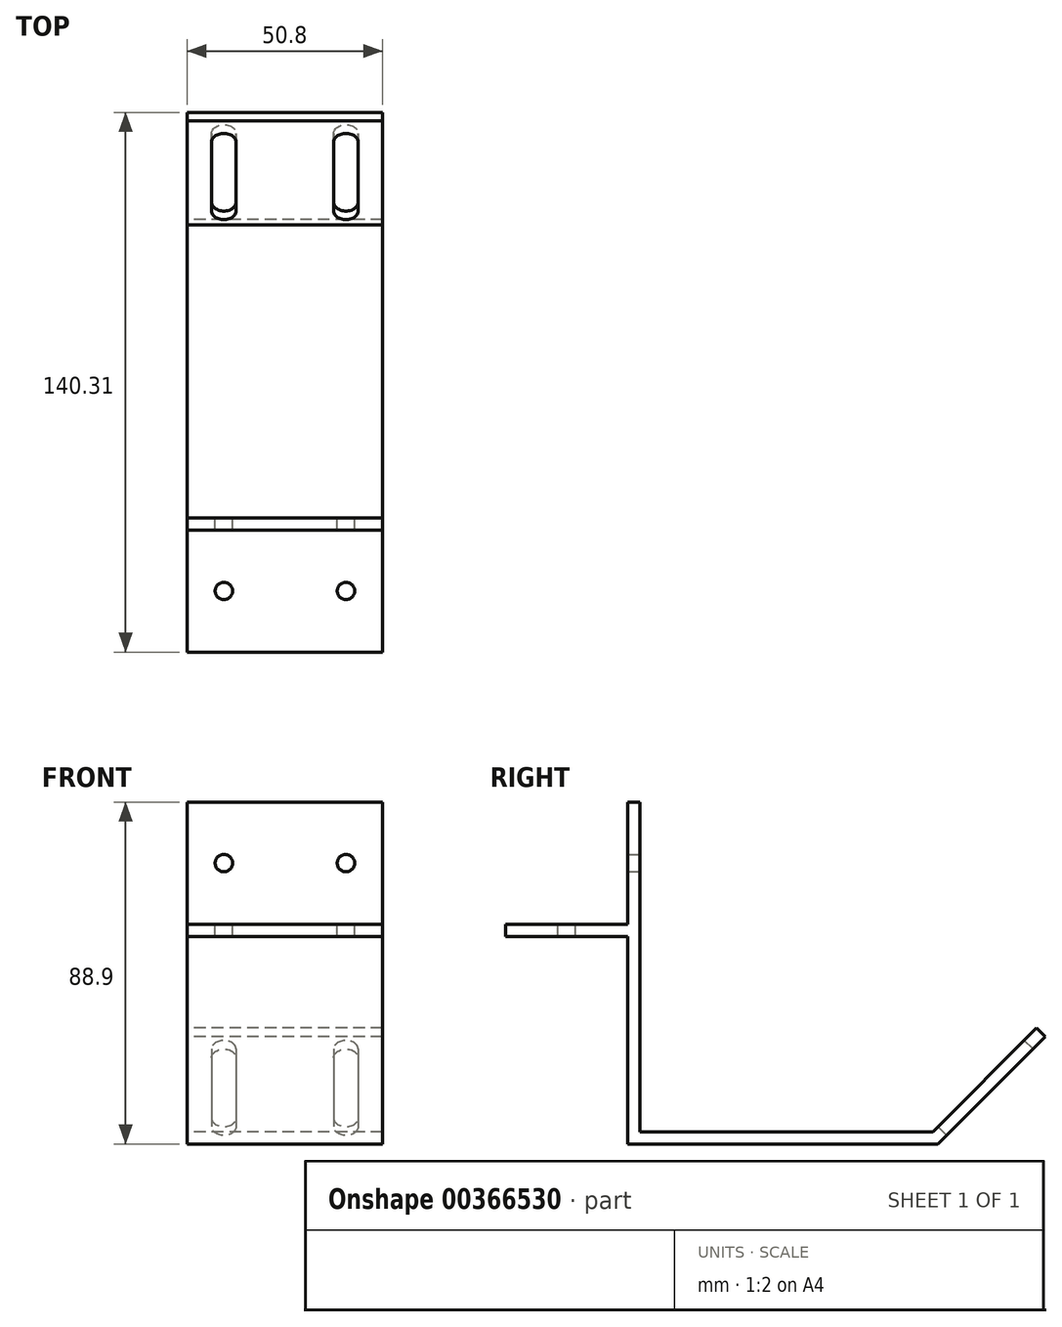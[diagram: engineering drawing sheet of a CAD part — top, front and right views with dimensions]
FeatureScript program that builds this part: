
annotation { "Feature Type Name" : "Feature", "Feature Type Description" : "" }
export const myFeature = defineFeature(function(context is Context, id is Id, definition is map)
    precondition{}
    {
        {
            var Q0;
            Q0=qCreatedBy(makeId("Right.planeOp"),FACE);
            var sketch = newSketch(context, id + "F0", { "sketchPlane" : qUnion([Q0])});
            skLineSegment(sketch, "E0", {"start": v(0, 0) * mm, "end": v(0, 31.75) * mm});
            skLineSegment(sketch, "E1", {"start": v(0, 0) * mm, "end": v(-31.75, 0) * mm});
            skLineSegment(sketch, "E2", {"start": v(-31.75, -3.18) * mm, "end": v(0, -3.18) * mm});
            skLineSegment(sketch, "E3", {"start": v(-31.75, 0) * mm, "end": v(-31.75, -3.17) * mm});
            skLineSegment(sketch, "E4", {"start": v(0, 31.75) * mm, "end": v(3.17, 31.75) * mm});
            skLineSegment(sketch, "E5", {"start": v(3.18, 31.75) * mm, "end": v(3.18, -53.98) * mm});
            skLineSegment(sketch, "E6", {"start": v(3.18, -53.98) * mm, "end": v(79.38, -53.97) * mm});
            skLineSegment(sketch, "E7", {"start": v(79.38, -53.97) * mm, "end": v(106.32, -27.03) * mm});
            skLineSegment(sketch, "E8", {"start": v(106.32, -27.03) * mm, "end": v(108.56, -29.28) * mm});
            skLineSegment(sketch, "E9", {"start": v(108.56, -29.28) * mm, "end": v(80.7, -57.15) * mm});
            skLineSegment(sketch, "E10", {"start": v(80.7, -57.15) * mm, "end": v(0, -57.15) * mm});
            skLineSegment(sketch, "E11", {"start": v(0, -57.15) * mm, "end": v(0, -3.18) * mm});
            skSolve(sketch);
        }
        {
            var Q0;
            Q0 = qSketchRegion(id + "F0", true);
            extrude(context, id + "F1", {"entities" : qUnion([Q0]), "endBound" : BoundingType.SYMMETRIC, "depth" : 50.8 * mm});
        }
        {
            var Q0;
            Q0=makeQuery(id+"F1.opExtrude","SWEPT_FACE",FACE,{"disambiguationData":[OSD([sQuery(id+"F0.wireOp",EDGE,"E5")])]});
            var sketch = newSketch(context, id + "F2", { "sketchPlane" : qUnion([Q0])});
            skCircle(sketch, "E12", {"center": v(15.88, 15.88) * mm, "radius": 2.26 * mm});
            skCircle(sketch, "E13", {"center": v(-15.88, 15.88) * mm, "radius": 2.26 * mm});
            skSolve(sketch);
        }
        {
            var Q0;
            Q0 = qSketchRegion(id + "F2", true);
            extrude(context, id + "F3", {"entities" : qUnion([Q0]), "operationType" : NewBodyOperationType.REMOVE, "endBound" : BoundingType.UP_TO_NEXT, "oppositeDirection" : true, "depth" : 25.4 * mm});
        }
        {
            var Q0;
            Q0=makeQuery(id+"F1.opExtrude","SWEPT_FACE",FACE,{"disambiguationData":[OSD([sQuery(id+"F0.wireOp",EDGE,"E1")])]});
            var sketch = newSketch(context, id + "F4", { "sketchPlane" : qUnion([Q0])});
            skCircle(sketch, "E14", {"center": v(15.88, -15.88) * mm, "radius": 2.26 * mm});
            skCircle(sketch, "E15", {"center": v(-15.88, -15.88) * mm, "radius": 2.26 * mm});
            skSolve(sketch);
        }
        {
            var Q0;
            Q0 = qSketchRegion(id + "F4", true);
            extrude(context, id + "F5", {"entities" : qUnion([Q0]), "operationType" : NewBodyOperationType.REMOVE, "endBound" : BoundingType.UP_TO_NEXT, "oppositeDirection" : true, "depth" : 25.4 * mm});
        }
        {
            var Q0;
            Q0=makeQuery(id+"F1.opExtrude","SWEPT_FACE",FACE,{"disambiguationData":[OSD([sQuery(id+"F0.wireOp",EDGE,"E9")])]});
            var sketch = newSketch(context, id + "F6", { "sketchPlane" : qUnion([Q0])});
            skLineSegment(sketch, "E16.bottom", {"start": v(-19.05, 48.37) * mm, "end": v(-12.7, 48.37) * mm});
            skLineSegment(sketch, "E16.top", {"start": v(-19.05, 22.97) * mm, "end": v(-12.7, 22.97) * mm});
            skLineSegment(sketch, "E16.left", {"start": v(-19.05, 48.37) * mm, "end": v(-19.05, 22.97) * mm});
            skLineSegment(sketch, "E16.right", {"start": v(-12.7, 48.37) * mm, "end": v(-12.7, 22.97) * mm});
            skLineSegment(sketch, "E17.bottom", {"start": v(12.7, 48.37) * mm, "end": v(19.05, 48.37) * mm});
            skLineSegment(sketch, "E17.top", {"start": v(12.7, 22.97) * mm, "end": v(19.05, 22.97) * mm});
            skLineSegment(sketch, "E17.left", {"start": v(12.7, 48.37) * mm, "end": v(12.7, 22.97) * mm});
            skLineSegment(sketch, "E17.right", {"start": v(19.05, 48.37) * mm, "end": v(19.05, 22.97) * mm});
            skLineSegment(sketch, "E18", {"start": v(0, 56.06) * mm, "end": v(0, 16.65) * mm, "construction": true});
            skArc(sketch, "E19", {"start": v(-12.7, 48.37) * mm, "mid": v(-15.88, 51.54) * mm, "end": v(-19.05, 48.37) * mm});
            skArc(sketch, "E20", {"start": v(-19.05, 22.97) * mm, "mid": v(-15.88, 19.8) * mm, "end": v(-12.7, 22.97) * mm});
            skArc(sketch, "E21", {"start": v(12.7, 22.97) * mm, "mid": v(15.87, 19.8) * mm, "end": v(19.05, 22.97) * mm});
            skArc(sketch, "E22", {"start": v(19.05, 48.37) * mm, "mid": v(15.87, 51.54) * mm, "end": v(12.7, 48.37) * mm});
            skSolve(sketch);
        }
        {
            var Q0;
            Q0 = qSketchRegion(id + "F6", true);
            extrude(context, id + "F7", {"entities" : qUnion([Q0]), "operationType" : NewBodyOperationType.REMOVE, "endBound" : BoundingType.UP_TO_NEXT, "oppositeDirection" : true, "depth" : 25.4 * mm});
        }
    });
